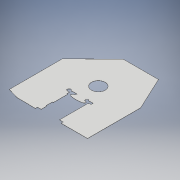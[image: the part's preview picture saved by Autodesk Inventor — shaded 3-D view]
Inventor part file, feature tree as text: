
AUTODESK INVENTOR PART (.ipt)
format: ipt  version: 2018 (Build 220112000, 112)  size: 224,768 bytes
history: native  units: mm
features: other x10, reference x8, extrude x3, sketch x3, plane x1
ambient origin geometry x8: Origin, YZ Plane, XZ Plane, XY Plane, X Axis, Y Axis, Z Axis, Center Point
bodies: Solid1 (feature_tree)
feature tree (25):
  other  "Table"
  other  "Cover V3-01"
  other  "Cover V3-02"
  plane  "Work Plane1"
  extrude  "Extrusion1"  Depth=500.0mm
  extrude  "Extrusion2"  Depth=530.0mm
  extrude  "Bed"  Depth=1.6mm
  sketch  "Sketch1"  dims[d9=815.0mm d10=500.0mm]
  reference  "Reference1"
  reference  "Reference2"
  reference  "Reference3"
  reference  "Reference4"
  reference  "Reference5"
  reference  "Reference6"
  reference  "Reference7"
  sketch  "Sketch2"  dims[d12=330.0mm d14=530.0mm]
  sketch  "Sketch3"  dims[d16=20.071286mm d17=1.6mm d22=1.6mm d23=0.0mm d25=300.0mm d26=1.6mm d27=0.0mm d28=2.0mm d29=1.6mm d30=0.0mm]
  reference  "Reference8"
  other  "Lathe Model 2018.iam"
  other  "front:1"
  other  "barrel:1"
  other  "X axis screw support:1"
  other  "chuck holder:1"
  other  "BED:1"
  other  "Gearbox:1"
